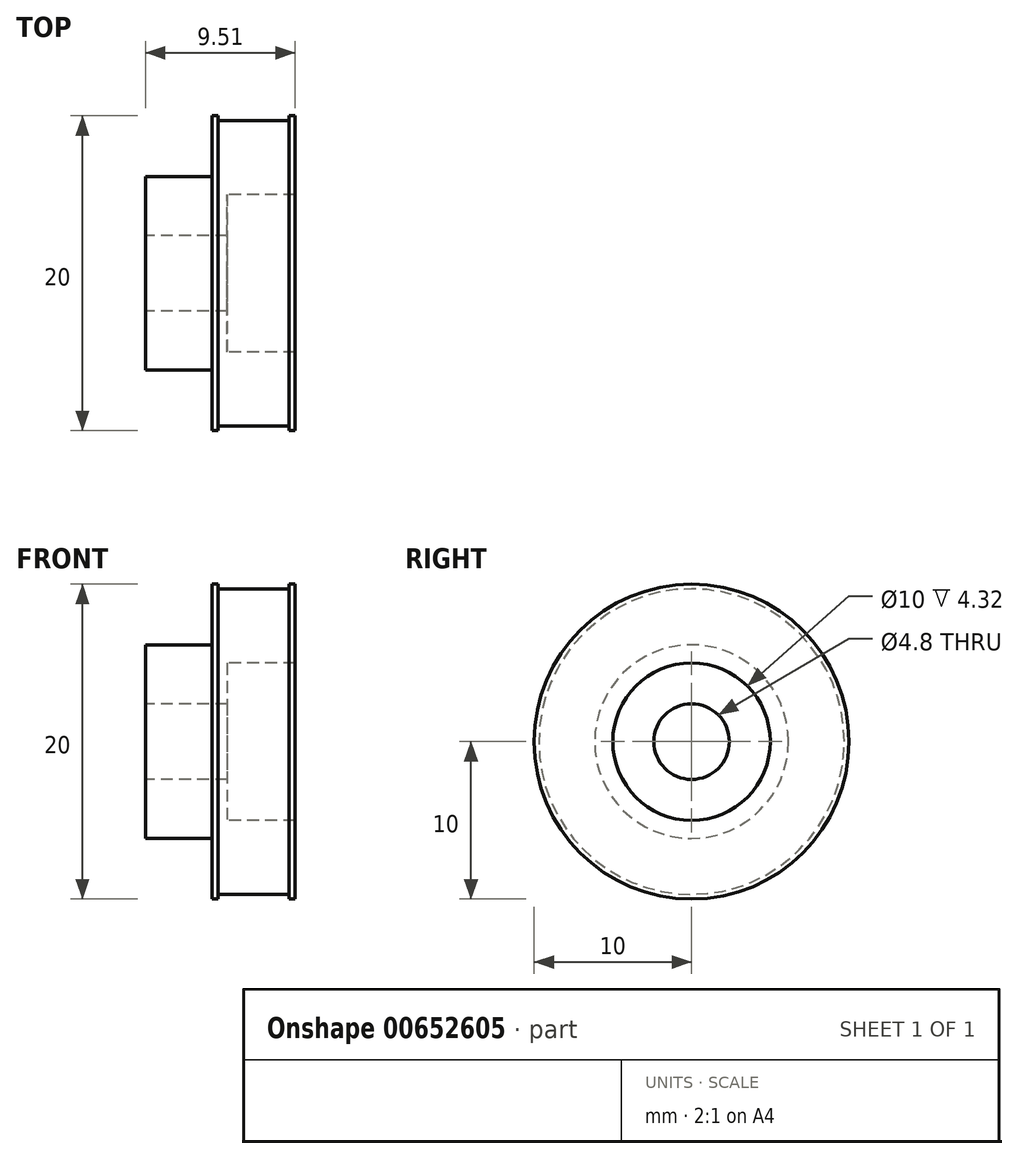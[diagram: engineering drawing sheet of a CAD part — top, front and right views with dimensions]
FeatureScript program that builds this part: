
annotation { "Feature Type Name" : "Feature", "Feature Type Description" : "" }
export const myFeature = defineFeature(function(context is Context, id is Id, definition is map)
    precondition{}
    {
        {
            var Q0;
            Q0=qCreatedBy(makeId("Front.planeOp"),FACE);
            var sketch = newSketch(context, id + "F0", { "sketchPlane" : qUnion([Q0])});
            skLineSegment(sketch, "E0", {"start": v(0, 0) * mm, "end": v(11.95, 0) * mm, "construction": true});
            skLineSegment(sketch, "E1", {"start": v(0, 2.4) * mm, "end": v(5.2, 2.4) * mm});
            skLineSegment(sketch, "E2", {"start": v(9.51, 5) * mm, "end": v(9.51, 10) * mm});
            skLineSegment(sketch, "E3", {"start": v(9.51, 10) * mm, "end": v(9.12, 10) * mm});
            skLineSegment(sketch, "E4", {"start": v(4.23, 10) * mm, "end": v(4.23, 6.15) * mm});
            skLineSegment(sketch, "E5", {"start": v(4.23, 6.15) * mm, "end": v(0, 6.15) * mm});
            skLineSegment(sketch, "E6", {"start": v(0, 6.15) * mm, "end": v(0, 2.4) * mm});
            skLineSegment(sketch, "E7", {"start": v(9.51, 5) * mm, "end": v(5.2, 5) * mm});
            skLineSegment(sketch, "E8", {"start": v(5.2, 5) * mm, "end": v(5.2, 2.4) * mm});
            skLineSegment(sketch, "E9", {"start": v(4.62, 10) * mm, "end": v(4.62, 9.7) * mm});
            skLineSegment(sketch, "E10", {"start": v(4.62, 9.7) * mm, "end": v(9.12, 9.7) * mm});
            skLineSegment(sketch, "E11", {"start": v(9.12, 9.7) * mm, "end": v(9.12, 10) * mm});
            skLineSegment(sketch, "E12.trimOffspring", {"start": v(4.62, 10) * mm, "end": v(4.23, 10) * mm});
            skSolve(sketch);
        }
        {
            var Q0;
            Q0 = qSketchRegion(id + "F0", true);
            var Q1;
            Q1=sQuery(id+"F0.wireOp",EDGE,"E0");
            revolve(context, id + "F1", {"entities" : qUnion([Q0]), "axis" : qUnion([Q1]), "revolveType" : RevolveType.FULL});
        }
    });
